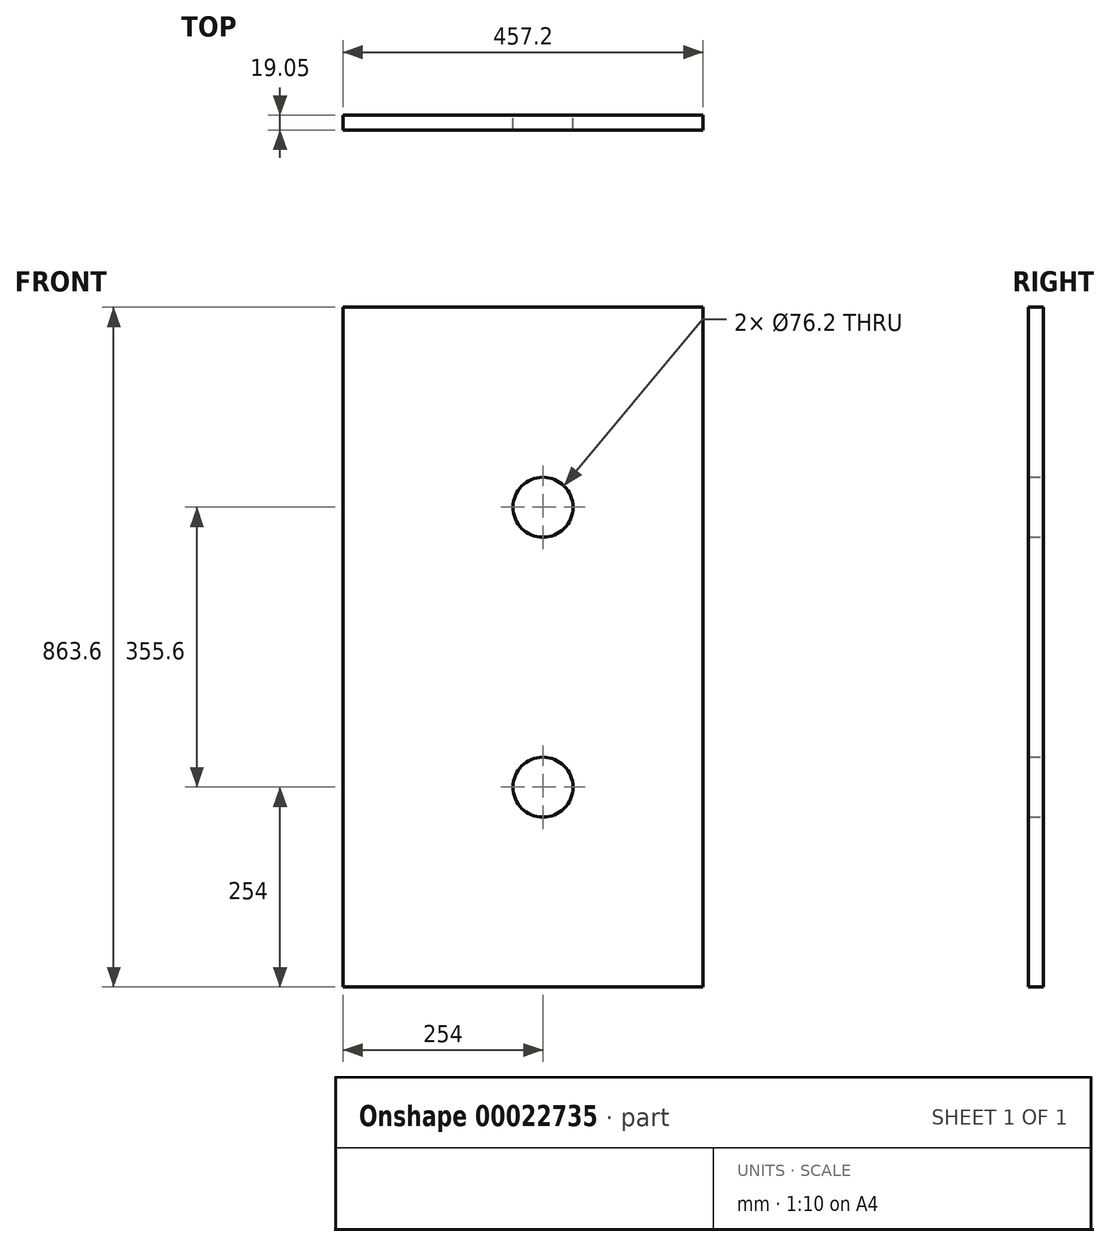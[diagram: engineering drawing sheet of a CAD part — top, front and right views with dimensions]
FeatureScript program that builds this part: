
annotation { "Feature Type Name" : "Feature", "Feature Type Description" : "" }
export const myFeature = defineFeature(function(context is Context, id is Id, definition is map)
    precondition{}
    {
        {
            var Q0;
            Q0=qCreatedBy(makeId("Front.planeOp"),FACE);
            var sketch = newSketch(context, id + "F0", { "sketchPlane" : qUnion([Q0])});
            skLineSegment(sketch, "E0.rect.bottom", {"start": v(203.2, 431.8) * mm, "end": v(-203.2, 431.8) * mm});
            skLineSegment(sketch, "E0.rect.top", {"start": v(203.2, -431.8) * mm, "end": v(-203.2, -431.8) * mm});
            skLineSegment(sketch, "E0.rect.left", {"start": v(203.2, 431.8) * mm, "end": v(203.2, -431.8) * mm});
            skLineSegment(sketch, "E0.rect.right", {"start": v(-203.2, 431.8) * mm, "end": v(-203.2, -431.8) * mm});
            skPoint(sketch, "E0.rect.middle", {"position": v(0, 0) * mm});
            skCircle(sketch, "E1", {"center": v(0, 177.8) * mm, "radius": 38.1 * mm});
            skCircle(sketch, "E2", {"center": v(0, -177.8) * mm, "radius": 38.1 * mm});
            skSolve(sketch);
        }
        {
            var Q0;
            Q0=makeQuery(id+"F0.imprint","IMPRINT",FACE,{"disambiguationData":[TD([[makeQuery(id+"F0.imprint","IMPRINT",EDGE,{"derivedFrom":sQuery(id+"F0.wireOp",EDGE,"E0.rect.bottom")}),1.0]])]});
            extrude(context, id + "F1", {"entities" : qUnion([Q0]), "depth" : 19.05 * mm});
        }
        {
            var Q0;
            Q0=makeQuery(id+"F1.opExtrude","SWEPT_FACE",FACE,{"disambiguationData":[OSD([sQuery(id+"F0.wireOp",EDGE,"E0.rect.right")])]});
            var sketch = newSketch(context, id + "F2", { "sketchPlane" : qUnion([Q0])});
            skLineSegment(sketch, "E3.bottom", {"start": v(0, 431.8) * mm, "end": v(19.05, 431.8) * mm});
            skLineSegment(sketch, "E3.top", {"start": v(0, -431.8) * mm, "end": v(19.05, -431.8) * mm});
            skLineSegment(sketch, "E3.left", {"start": v(0, 431.8) * mm, "end": v(0, -431.8) * mm});
            skLineSegment(sketch, "E3.right", {"start": v(19.05, 431.8) * mm, "end": v(19.05, -431.8) * mm});
            skSolve(sketch);
        }
        {
            var Q0;
            Q0 = qSketchRegion(id + "F2", true);
            extrude(context, id + "F3", {"entities" : qUnion([Q0]), "operationType" : NewBodyOperationType.ADD, "depth" : 50.8 * mm});
        }
    });
